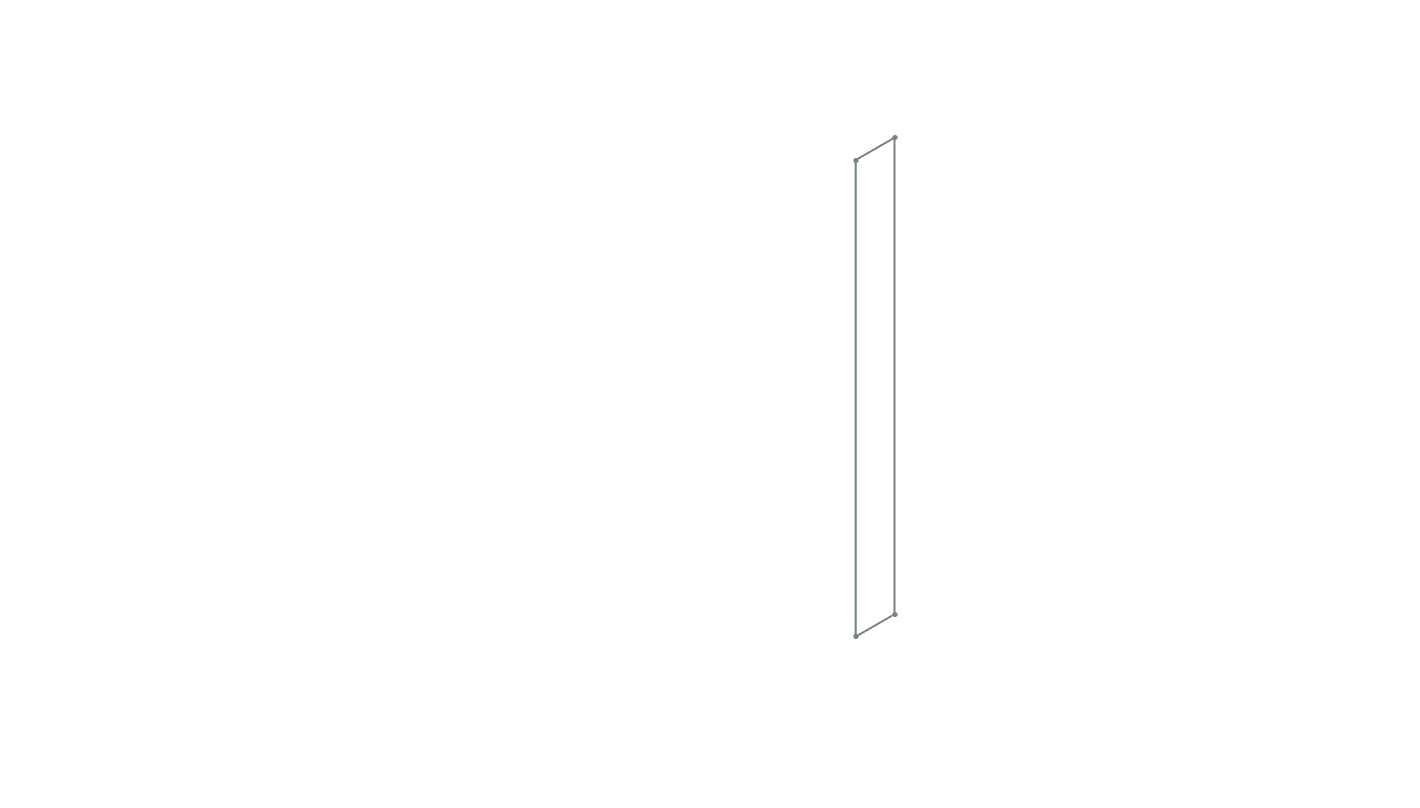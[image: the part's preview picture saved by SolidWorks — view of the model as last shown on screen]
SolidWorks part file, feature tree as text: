
SOLIDWORKS PART (.sldprt)
format: sldprt  version: not decoded by parser v0  size: 359,936 bytes
history: native  units: mm
features: sketch x14, cut_extrude x6, plane x3, hole x3, extrude x2, material x1 (+9 scaffold rows collapsed)
feature tree (38):
  scaffold x9  (default folders/planes/origin — collapsed)
  material  "Acier non allié"
  plane  "Plan de face"
  plane  "Plan de dessus"
  plane  "Plan de droite"
  sketch  "Esquisse1"  dims[c1.D1=42.5mm c1.D2=~9.216466mm c2.D1=14.0mm c2.D2=4.0mm c2.D3=~10.77033mm c3.D3=90.0deg]
  extrude  "Boss.-Extru.1"  Depth=4mm
  sketch  "Esquisse2"  dims[c1.D1=42.5mm c1.D2=~4.922223mm c2.D1=8.0mm]
  extrude  "Boss.-Extru.2"  Depth=24mm
  sketch  "Esquisse3"  dims[D1=~12.347234mm D2=9.0mm]
  cut_extrude  "Enlèv. mat.-Extru.1"  [1 undecoded]
  sketch  "Esquisse7"  dims[D1=11.0mm]
  cut_extrude  "Enlèv. mat.-Extru.3"  [1 undecoded]
  sketch  "Esquisse8"  dims[D1=0.0mm]
  cut_extrude  "Enlèv. mat.-Extru.4"  [1 undecoded]
  sketch  "Esquisse6"  dims[c1.D1=~9.020082mm c1.D2=~10.758098mm c2.D1=~10.926647mm c2.D2=~10.758098mm c3.D1=12.0mm c3.D2=7.0mm]
  cut_extrude  "Enlèv. mat.-Extru.2"  [1 undecoded]
  hole  "Chambrage pour vis à tête hexagonale M31"  Diameter=3.4mm Depth=30mm
  sketch  "Esquisse11"  dims[D1=2.5mm D2=6.4mm]
  sketch  "Esquisse12"  dims[hole-wizard template sketch: 28 standard entries collapsed; hole parameters kept: c8.Diamètre du perçage=3.4mm c8.Profondeur du perçage=30.0mm c8.Diamètre du chambrage=6.5mm c8.Profondeur du chambrage=3.4mm c8.D5=~14.816244mm c8.Angle de pointe=118.0deg]
  hole  "Trou pour taraudage pour trou taraudé M31"  Diameter=2.5mm Depth=34.5mm
  sketch  "Esquisse14"  dims[D1=4.0mm D2=4.0mm D3=34.5mm]
  sketch  "Esquisse13"  dims[hole-wizard template sketch: 47 standard entries collapsed; hole parameters kept: c15.Profondeur du perçage=34.5mm c15.D3=~14.816244mm c15.Angle de pointe=180.0deg]
  sketch  "Esquisse15"  dims[D1=5.4mm]
  cut_extrude  "Enlèv. mat.-Extru.5"  Depth=4.1mm
  sketch  "Esquisse16"  dims[D1=2.0mm D2=40.0mm]
  cut_extrude  "Enlèv. mat.-Extru.6"  [1 undecoded]
  hole  "Trou pour taraudage pour trou taraudé M32"  Diameter=2.5mm Depth=5mm
  sketch  "Esquisse18"  dims[D1=24.0mm]
  sketch  "Esquisse17"  dims[hole-wizard template sketch: 47 standard entries collapsed; hole parameters kept: c15.Profondeur du perçage=5.0mm c15.D3=~14.816244mm c15.Angle de pointe=180.0deg]
decode coverage: 20 of 25 modeling features carry decoded parameters
note: ~ marks probable driven/reference dimensions
note: 5 parameter values undecoded
summary: no parameter record found for 5 features
note: suppression state not decoded; provenance and decode notes live in map.json
